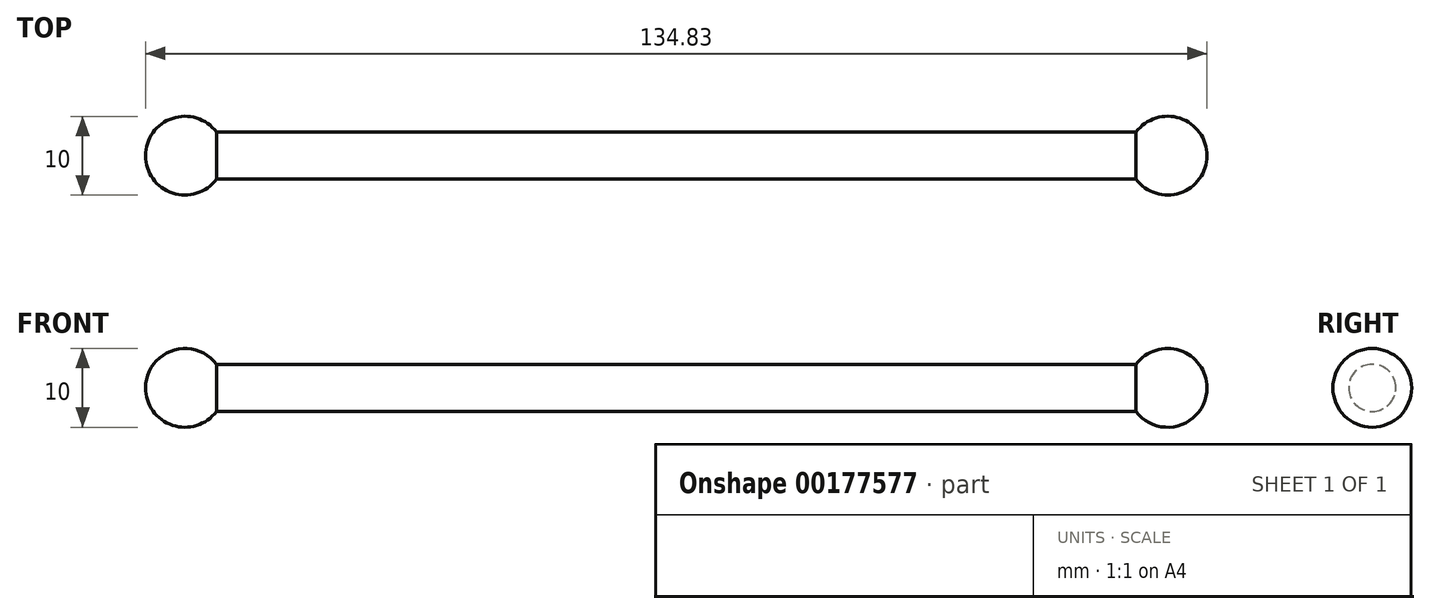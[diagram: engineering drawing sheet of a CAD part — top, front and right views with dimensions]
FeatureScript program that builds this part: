
annotation { "Feature Type Name" : "Feature", "Feature Type Description" : "" }
export const myFeature = defineFeature(function(context is Context, id is Id, definition is map)
    precondition{}
    {
        {
            var Q0;
            Q0=qCreatedBy(makeId("Front.planeOp"),FACE);
            var sketch = newSketch(context, id + "F0", { "sketchPlane" : qUnion([Q0])});
            skLineSegment(sketch, "E0", {"start": v(0, 0) * mm, "end": v(-18.8, 0) * mm});
            skLineSegment(sketch, "E1", {"start": v(0, 0) * mm, "end": v(0, -3) * mm});
            skLineSegment(sketch, "E2.0", {"start": v(0, -3) * mm, "end": v(-116.84, -3) * mm});
            skArc(sketch, "E3", {"start": v(-124.65, -3.24) * mm, "mid": v(-120.69, -5) * mm, "end": v(-116.84, -3) * mm});
            skArc(sketch, "E4", {"start": v(-125.84, 0) * mm, "mid": v(-122.42, -4.74) * mm, "end": v(-116.84, -3) * mm});
            skLineSegment(sketch, "E5", {"start": v(-18.8, 0) * mm, "end": v(-125.84, 0) * mm});
            skArc(sketch, "E6", {"start": v(-0.02, -3) * mm, "mid": v(5.57, -4.75) * mm, "end": v(9, 0) * mm});
            skLineSegment(sketch, "E7", {"start": v(0, 0) * mm, "end": v(9, 0) * mm});
            skSolve(sketch);
        }
        {
            var Q0;
            Q0=qSketchRegion(id+"F0",true);
            var Q1;
            Q1=sQuery(id+"F0.wireOp",EDGE,"E0");
            revolve(context, id + "F1", {"entities" : qUnion([Q0]), "axis" : qUnion([Q1]), "revolveType" : RevolveType.FULL});
        }
    });
